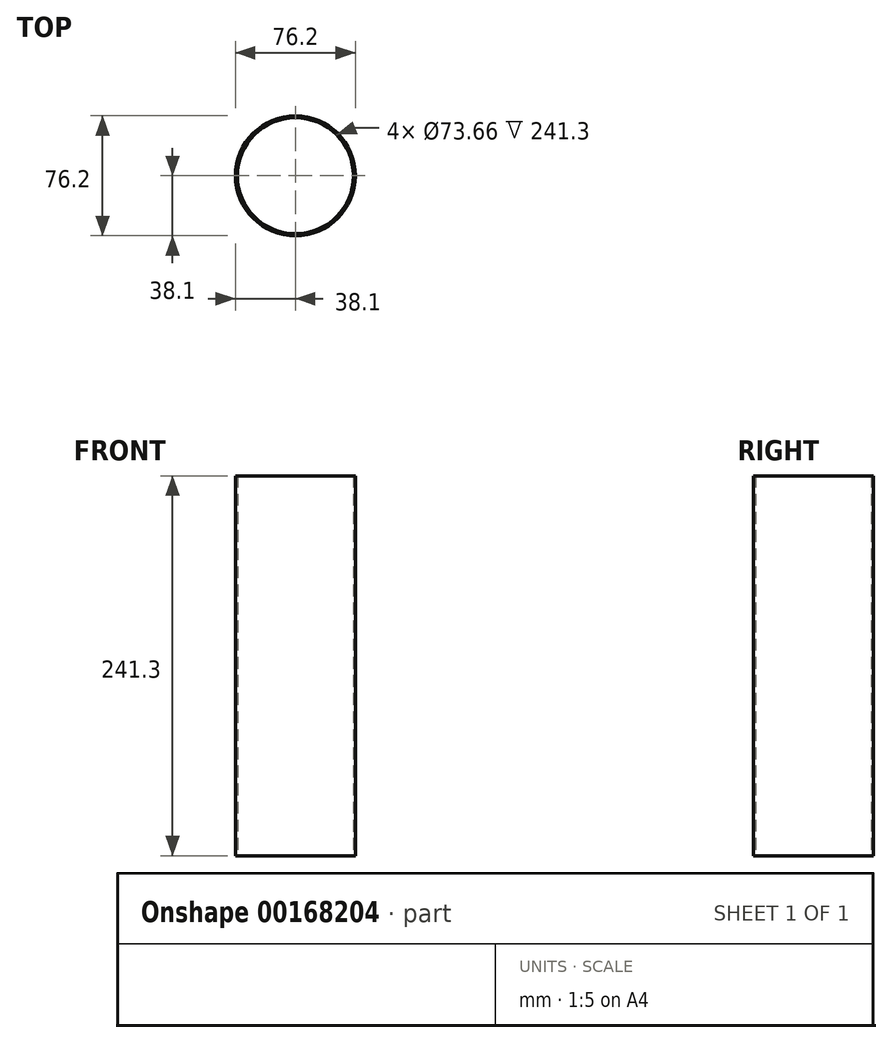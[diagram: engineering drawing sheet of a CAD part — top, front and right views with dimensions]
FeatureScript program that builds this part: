
annotation { "Feature Type Name" : "Feature", "Feature Type Description" : "" }
export const myFeature = defineFeature(function(context is Context, id is Id, definition is map)
    precondition{}
    {
        {
            var Q0;
            Q0=qCreatedBy(makeId("Top.planeOp"),FACE);
            var sketch = newSketch(context, id + "F0", { "sketchPlane" : qUnion([Q0])});
            skCircle(sketch, "E0", {"center": v(0, 0) * mm, "radius": 36.83 * mm});
            skCircle(sketch, "E1", {"center": v(0, 0) * mm, "radius": 38.1 * mm});
            skSolve(sketch);
        }
        {
            var Q0;
            Q0 = qSketchRegion(id + "F0", true);
            extrude(context, id + "F1", {"entities" : qUnion([Q0]), "depth" : 241.3 * mm});
        }
    });
